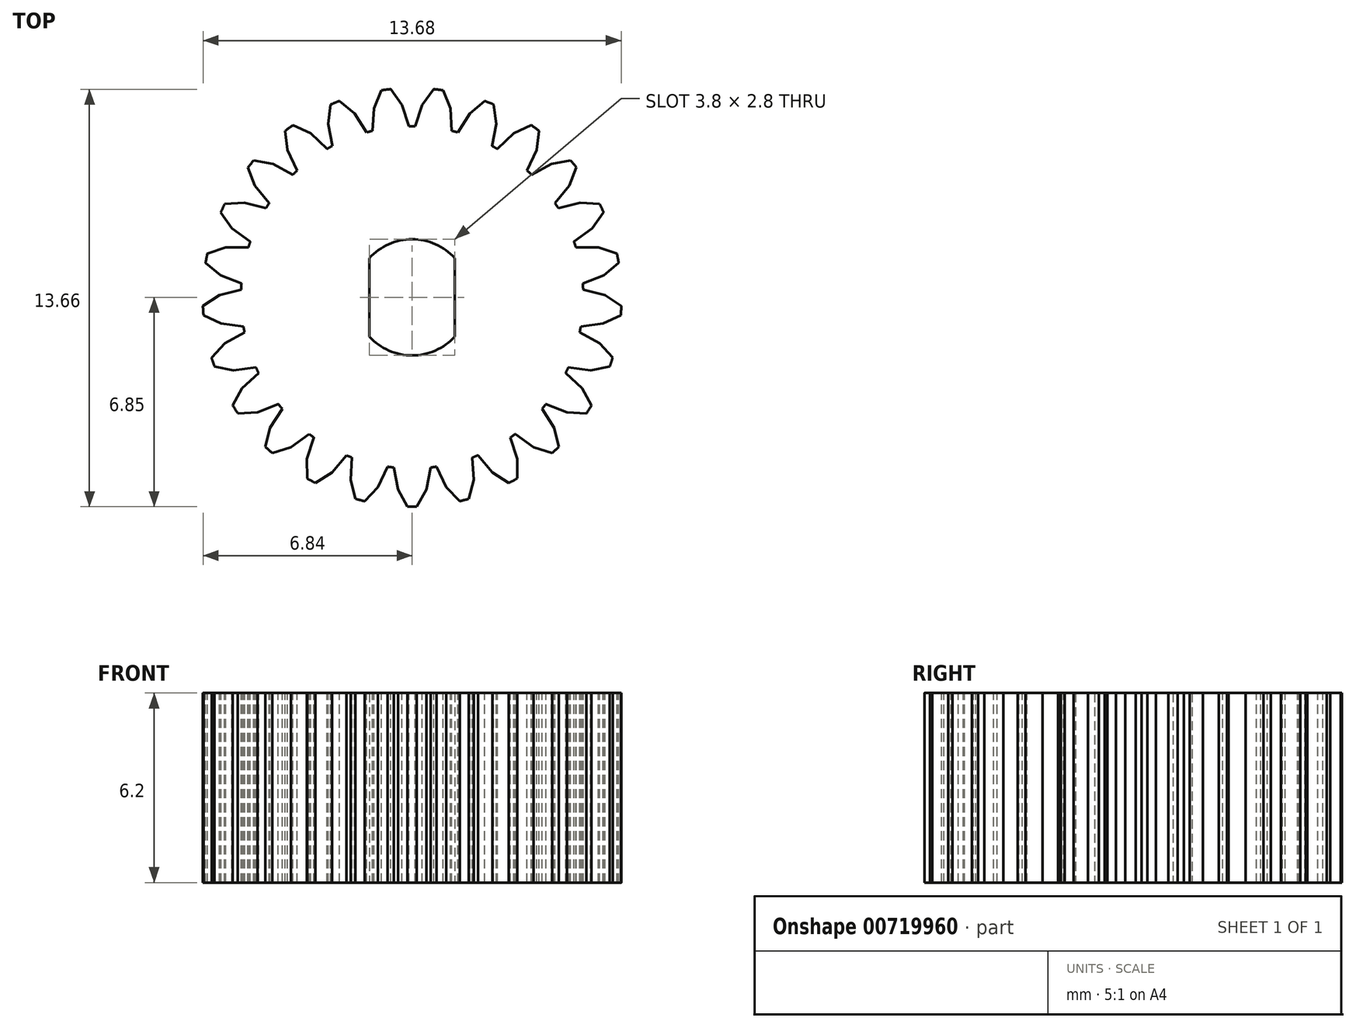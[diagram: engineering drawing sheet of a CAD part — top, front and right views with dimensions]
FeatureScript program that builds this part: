
annotation { "Feature Type Name" : "Feature", "Feature Type Description" : "" }
export const myFeature = defineFeature(function(context is Context, id is Id, definition is map)
    precondition{}
    {
        {
            var Q0;
            Q0=qCreatedBy(makeId("Top.planeOp"),FACE);
            var sketch = newSketch(context, id + "F0", { "sketchPlane" : qUnion([Q0])});
            skCircle(sketch, "E0", {"center": v(0, 0) * mm, "radius": 6.85 * mm});
            skArc(sketch, "E1", {"start": v(-1.4, -1.28) * mm, "mid": v(0, -1.9) * mm, "end": v(1.4, -1.28) * mm});
            skLineSegment(sketch, "E2.left", {"start": v(-1.4, 1.28) * mm, "end": v(-1.4, -1.28) * mm});
            skLineSegment(sketch, "E2.right", {"start": v(1.4, 1.28) * mm, "end": v(1.4, -1.28) * mm});
            skArc(sketch, "E3.trimOffspring", {"start": v(1.4, 1.28) * mm, "mid": v(0, 1.9) * mm, "end": v(-1.4, 1.28) * mm});
            skSolve(sketch);
        }
        {
            var Q0;
            Q0 = qSketchRegion(id + "F0", true);
            extrude(context, id + "F1", {"entities" : qUnion([Q0]), "depth" : 6.2 * mm, "offsetDistance" : 25 * mm});
        }
        {
            var Q0;
            Q0=makeQuery(id+"F1.opExtrude","CAP_FACE",FACE,{"disambiguationData":[OSD([sQuery(id+"F0.wireOp",EDGE,"E0"),sQuery(id+"F0.wireOp",EDGE,"E1"),sQuery(id+"F0.wireOp",EDGE,"E2.left"),sQuery(id+"F0.wireOp",EDGE,"E2.right"),sQuery(id+"F0.wireOp",EDGE,"E3.trimOffspring")])],"isStart":false});
            var sketch = newSketch(context, id + "F2", { "sketchPlane" : qUnion([Q0])});
            skArc(sketch, "E4.0", {"start": v(0.7, 6.81) * mm, "mid": v(0, 6.85) * mm, "end": v(-0.7, 6.81) * mm});
            skPoint(sketch, "E5.orphan", {"position": v(0, 5.3) * mm});
            skArc(sketch, "E6.trimOffspring", {"start": v(0.1, 5.6) * mm, "mid": v(0, 5.6) * mm, "end": v(-0.1, 5.6) * mm});
            skLineSegment(sketch, "E7", {"start": v(-0.7, 6.81) * mm, "end": v(-0.33, 6.3) * mm});
            skLineSegment(sketch, "E8", {"start": v(-0.1, 5.6) * mm, "end": v(-0.33, 6.3) * mm});
            skLineSegment(sketch, "E9.MirrorCS", {"start": v(0.7, 6.81) * mm, "end": v(0.33, 6.3) * mm});
            skLineSegment(sketch, "E10.MirrorCS", {"start": v(0.1, 5.6) * mm, "end": v(0.33, 6.3) * mm});
            skLineSegment(sketch, "E11.1.0", {"start": v(-2.38, 6.42) * mm, "end": v(-1.88, 6.02) * mm});
            skArc(sketch, "E11.1.1", {"start": v(-1.01, 6.78) * mm, "mid": v(-1.7, 6.63) * mm, "end": v(-2.38, 6.42) * mm});
            skLineSegment(sketch, "E11.1.2", {"start": v(-1.01, 6.78) * mm, "end": v(-1.25, 6.18) * mm});
            skLineSegment(sketch, "E11.1.3", {"start": v(-1.3, 5.45) * mm, "end": v(-1.25, 6.18) * mm});
            skLineSegment(sketch, "E11.1.4", {"start": v(-1.49, 5.4) * mm, "end": v(-1.88, 6.02) * mm});
            skArc(sketch, "E11.1.5", {"start": v(-1.22, 5.47) * mm, "mid": v(-1.35, 5.43) * mm, "end": v(-1.49, 5.4) * mm});
            skLineSegment(sketch, "E11.2.0", {"start": v(-3.9, 5.63) * mm, "end": v(-3.32, 5.36) * mm});
            skArc(sketch, "E11.2.1", {"start": v(-2.66, 6.31) * mm, "mid": v(-3.3, 6) * mm, "end": v(-3.9, 5.63) * mm});
            skLineSegment(sketch, "E11.2.2", {"start": v(-2.66, 6.31) * mm, "end": v(-2.75, 5.68) * mm});
            skLineSegment(sketch, "E11.2.3", {"start": v(-2.6, 4.95) * mm, "end": v(-2.75, 5.68) * mm});
            skLineSegment(sketch, "E11.2.4", {"start": v(-2.78, 4.86) * mm, "end": v(-3.32, 5.36) * mm});
            skArc(sketch, "E11.2.5", {"start": v(-2.54, 5) * mm, "mid": v(-2.66, 4.93) * mm, "end": v(-2.78, 4.86) * mm});
            skLineSegment(sketch, "E11.3.0", {"start": v(-5.18, 4.48) * mm, "end": v(-4.55, 4.37) * mm});
            skArc(sketch, "E11.3.1", {"start": v(-4.15, 5.45) * mm, "mid": v(-4.69, 5) * mm, "end": v(-5.18, 4.48) * mm});
            skLineSegment(sketch, "E11.3.2", {"start": v(-4.15, 5.45) * mm, "end": v(-4.07, 4.82) * mm});
            skLineSegment(sketch, "E11.3.3", {"start": v(-3.76, 4.15) * mm, "end": v(-4.07, 4.82) * mm});
            skLineSegment(sketch, "E11.3.4", {"start": v(-3.9, 4.01) * mm, "end": v(-4.55, 4.37) * mm});
            skArc(sketch, "E11.3.5", {"start": v(-3.7, 4.2) * mm, "mid": v(-3.8, 4.1) * mm, "end": v(-3.9, 4.01) * mm});
            skLineSegment(sketch, "E11.4.0", {"start": v(-6.13, 3.05) * mm, "end": v(-5.5, 3.1) * mm});
            skArc(sketch, "E11.4.1", {"start": v(-5.37, 4.25) * mm, "mid": v(-5.78, 3.67) * mm, "end": v(-6.13, 3.05) * mm});
            skLineSegment(sketch, "E11.4.2", {"start": v(-5.37, 4.25) * mm, "end": v(-5.14, 3.65) * mm});
            skLineSegment(sketch, "E11.4.3", {"start": v(-4.67, 3.08) * mm, "end": v(-5.14, 3.65) * mm});
            skLineSegment(sketch, "E11.4.4", {"start": v(-4.78, 2.92) * mm, "end": v(-5.5, 3.1) * mm});
            skArc(sketch, "E11.4.5", {"start": v(-4.63, 3.15) * mm, "mid": v(-4.7, 3.03) * mm, "end": v(-4.78, 2.92) * mm});
            skLineSegment(sketch, "E11.5.0", {"start": v(-6.7, 1.43) * mm, "end": v(-6.1, 1.63) * mm});
            skArc(sketch, "E11.5.1", {"start": v(-6.26, 2.78) * mm, "mid": v(-6.51, 2.12) * mm, "end": v(-6.7, 1.43) * mm});
            skLineSegment(sketch, "E11.5.2", {"start": v(-6.26, 2.78) * mm, "end": v(-5.9, 2.26) * mm});
            skLineSegment(sketch, "E11.5.3", {"start": v(-5.3, 1.83) * mm, "end": v(-5.9, 2.26) * mm});
            skLineSegment(sketch, "E11.5.4", {"start": v(-5.36, 1.63) * mm, "end": v(-6.1, 1.63) * mm});
            skArc(sketch, "E11.5.5", {"start": v(-5.27, 1.9) * mm, "mid": v(-5.31, 1.77) * mm, "end": v(-5.36, 1.63) * mm});
            skLineSegment(sketch, "E11.6.0", {"start": v(-6.84, -0.28) * mm, "end": v(-6.3, 0.07) * mm});
            skArc(sketch, "E11.6.1", {"start": v(-6.76, 1.13) * mm, "mid": v(-6.84, 0.43) * mm, "end": v(-6.84, -0.28) * mm});
            skLineSegment(sketch, "E11.6.2", {"start": v(-6.76, 1.13) * mm, "end": v(-6.27, 0.72) * mm});
            skLineSegment(sketch, "E11.6.3", {"start": v(-5.58, 0.45) * mm, "end": v(-6.27, 0.72) * mm});
            skLineSegment(sketch, "E11.6.4", {"start": v(-5.6, 0.25) * mm, "end": v(-6.3, 0.07) * mm});
            skArc(sketch, "E11.6.5", {"start": v(-5.58, 0.53) * mm, "mid": v(-5.59, 0.4) * mm, "end": v(-5.6, 0.25) * mm});
            skLineSegment(sketch, "E11.7.0", {"start": v(-6.56, -1.97) * mm, "end": v(-6.13, -1.5) * mm});
            skArc(sketch, "E11.7.1", {"start": v(-6.83, -0.58) * mm, "mid": v(-6.73, -1.28) * mm, "end": v(-6.56, -1.97) * mm});
            skLineSegment(sketch, "E11.7.2", {"start": v(-6.83, -0.58) * mm, "end": v(-6.25, -0.86) * mm});
            skLineSegment(sketch, "E11.7.3", {"start": v(-5.52, -0.95) * mm, "end": v(-6.25, -0.86) * mm});
            skLineSegment(sketch, "E11.7.4", {"start": v(-5.48, -1.15) * mm, "end": v(-6.13, -1.5) * mm});
            skArc(sketch, "E11.7.5", {"start": v(-5.53, -0.87) * mm, "mid": v(-5.5, -1.01) * mm, "end": v(-5.48, -1.15) * mm});
            skLineSegment(sketch, "E11.8.0", {"start": v(-5.86, -3.54) * mm, "end": v(-5.56, -2.98) * mm});
            skArc(sketch, "E11.8.1", {"start": v(-6.47, -2.26) * mm, "mid": v(-6.2, -2.92) * mm, "end": v(-5.86, -3.54) * mm});
            skLineSegment(sketch, "E11.8.2", {"start": v(-6.47, -2.26) * mm, "end": v(-5.84, -2.39) * mm});
            skLineSegment(sketch, "E11.8.3", {"start": v(-5.1, -2.3) * mm, "end": v(-5.84, -2.39) * mm});
            skLineSegment(sketch, "E11.8.4", {"start": v(-5.02, -2.47) * mm, "end": v(-5.56, -2.98) * mm});
            skArc(sketch, "E11.8.5", {"start": v(-5.14, -2.22) * mm, "mid": v(-5.08, -2.35) * mm, "end": v(-5.02, -2.47) * mm});
            skLineSegment(sketch, "E11.9.0", {"start": v(-4.8, -4.89) * mm, "end": v(-4.65, -4.27) * mm});
            skArc(sketch, "E11.9.1", {"start": v(-5.7, -3.8) * mm, "mid": v(-5.28, -4.37) * mm, "end": v(-4.8, -4.89) * mm});
            skLineSegment(sketch, "E11.9.2", {"start": v(-5.7, -3.8) * mm, "end": v(-5.06, -3.76) * mm});
            skLineSegment(sketch, "E11.9.3", {"start": v(-4.38, -3.5) * mm, "end": v(-5.06, -3.76) * mm});
            skLineSegment(sketch, "E11.9.4", {"start": v(-4.25, -3.65) * mm, "end": v(-4.65, -4.27) * mm});
            skArc(sketch, "E11.9.5", {"start": v(-4.43, -3.43) * mm, "mid": v(-4.34, -3.54) * mm, "end": v(-4.25, -3.65) * mm});
            skLineSegment(sketch, "E11.10.0", {"start": v(-3.43, -5.93) * mm, "end": v(-3.44, -5.29) * mm});
            skArc(sketch, "E11.10.1", {"start": v(-4.58, -5.1) * mm, "mid": v(-4.03, -5.54) * mm, "end": v(-3.43, -5.93) * mm});
            skLineSegment(sketch, "E11.10.2", {"start": v(-4.58, -5.1) * mm, "end": v(-3.97, -4.9) * mm});
            skLineSegment(sketch, "E11.10.3", {"start": v(-3.37, -4.47) * mm, "end": v(-3.97, -4.9) * mm});
            skLineSegment(sketch, "E11.10.4", {"start": v(-3.2, -4.59) * mm, "end": v(-3.44, -5.29) * mm});
            skArc(sketch, "E11.10.5", {"start": v(-3.43, -4.42) * mm, "mid": v(-3.32, -4.5) * mm, "end": v(-3.2, -4.59) * mm});
            skLineSegment(sketch, "E11.11.0", {"start": v(-1.85, -6.6) * mm, "end": v(-2.01, -5.98) * mm});
            skArc(sketch, "E11.11.1", {"start": v(-3.16, -6.08) * mm, "mid": v(-2.52, -6.37) * mm, "end": v(-1.85, -6.6) * mm});
            skLineSegment(sketch, "E11.11.2", {"start": v(-3.16, -6.08) * mm, "end": v(-2.62, -5.74) * mm});
            skLineSegment(sketch, "E11.11.3", {"start": v(-2.15, -5.17) * mm, "end": v(-2.62, -5.74) * mm});
            skLineSegment(sketch, "E11.11.4", {"start": v(-1.97, -5.24) * mm, "end": v(-2.01, -5.98) * mm});
            skArc(sketch, "E11.11.5", {"start": v(-2.23, -5.14) * mm, "mid": v(-2.1, -5.2) * mm, "end": v(-1.97, -5.24) * mm});
            skLineSegment(sketch, "E11.12.0", {"start": v(-0.15, -6.85) * mm, "end": v(-0.46, -6.3) * mm});
            skArc(sketch, "E11.12.1", {"start": v(-1.55, -6.67) * mm, "mid": v(-0.86, -6.8) * mm, "end": v(-0.15, -6.85) * mm});
            skLineSegment(sketch, "E11.12.2", {"start": v(-1.55, -6.67) * mm, "end": v(-1.12, -6.2) * mm});
            skLineSegment(sketch, "E11.12.3", {"start": v(-0.8, -5.54) * mm, "end": v(-1.12, -6.2) * mm});
            skLineSegment(sketch, "E11.12.4", {"start": v(-0.6, -5.57) * mm, "end": v(-0.46, -6.3) * mm});
            skArc(sketch, "E11.12.5", {"start": v(-0.88, -5.53) * mm, "mid": v(-0.74, -5.55) * mm, "end": v(-0.6, -5.57) * mm});
            skLineSegment(sketch, "E11.13.0", {"start": v(1.55, -6.67) * mm, "end": v(1.12, -6.2) * mm});
            skArc(sketch, "E11.13.1", {"start": v(0.15, -6.85) * mm, "mid": v(0.86, -6.8) * mm, "end": v(1.55, -6.67) * mm});
            skLineSegment(sketch, "E11.13.2", {"start": v(0.15, -6.85) * mm, "end": v(0.46, -6.3) * mm});
            skLineSegment(sketch, "E11.13.3", {"start": v(0.6, -5.57) * mm, "end": v(0.46, -6.3) * mm});
            skLineSegment(sketch, "E11.13.4", {"start": v(0.8, -5.54) * mm, "end": v(1.12, -6.2) * mm});
            skArc(sketch, "E11.13.5", {"start": v(0.52, -5.58) * mm, "mid": v(0.66, -5.56) * mm, "end": v(0.8, -5.54) * mm});
            skLineSegment(sketch, "E11.14.0", {"start": v(3.16, -6.08) * mm, "end": v(2.62, -5.74) * mm});
            skArc(sketch, "E11.14.1", {"start": v(1.85, -6.6) * mm, "mid": v(2.52, -6.37) * mm, "end": v(3.16, -6.08) * mm});
            skLineSegment(sketch, "E11.14.2", {"start": v(1.85, -6.6) * mm, "end": v(2.01, -5.98) * mm});
            skLineSegment(sketch, "E11.14.3", {"start": v(1.97, -5.24) * mm, "end": v(2.01, -5.98) * mm});
            skLineSegment(sketch, "E11.14.4", {"start": v(2.15, -5.17) * mm, "end": v(2.62, -5.74) * mm});
            skArc(sketch, "E11.14.5", {"start": v(1.9, -5.27) * mm, "mid": v(2.03, -5.22) * mm, "end": v(2.15, -5.17) * mm});
            skLineSegment(sketch, "E11.15.0", {"start": v(4.58, -5.1) * mm, "end": v(3.97, -4.9) * mm});
            skArc(sketch, "E11.15.1", {"start": v(3.43, -5.93) * mm, "mid": v(4.03, -5.54) * mm, "end": v(4.58, -5.1) * mm});
            skLineSegment(sketch, "E11.15.2", {"start": v(3.43, -5.93) * mm, "end": v(3.44, -5.29) * mm});
            skLineSegment(sketch, "E11.15.3", {"start": v(3.2, -4.59) * mm, "end": v(3.44, -5.29) * mm});
            skLineSegment(sketch, "E11.15.4", {"start": v(3.37, -4.47) * mm, "end": v(3.97, -4.9) * mm});
            skArc(sketch, "E11.15.5", {"start": v(3.15, -4.63) * mm, "mid": v(3.26, -4.55) * mm, "end": v(3.37, -4.47) * mm});
            skLineSegment(sketch, "E11.16.0", {"start": v(5.7, -3.8) * mm, "end": v(5.06, -3.76) * mm});
            skArc(sketch, "E11.16.1", {"start": v(4.8, -4.89) * mm, "mid": v(5.28, -4.37) * mm, "end": v(5.7, -3.8) * mm});
            skLineSegment(sketch, "E11.16.2", {"start": v(4.8, -4.89) * mm, "end": v(4.65, -4.27) * mm});
            skLineSegment(sketch, "E11.16.3", {"start": v(4.25, -3.65) * mm, "end": v(4.65, -4.27) * mm});
            skLineSegment(sketch, "E11.16.4", {"start": v(4.38, -3.5) * mm, "end": v(5.06, -3.76) * mm});
            skArc(sketch, "E11.16.5", {"start": v(4.2, -3.7) * mm, "mid": v(4.29, -3.6) * mm, "end": v(4.38, -3.5) * mm});
            skLineSegment(sketch, "E11.17.0", {"start": v(6.47, -2.26) * mm, "end": v(5.84, -2.39) * mm});
            skArc(sketch, "E11.17.1", {"start": v(5.86, -3.54) * mm, "mid": v(6.2, -2.92) * mm, "end": v(6.47, -2.26) * mm});
            skLineSegment(sketch, "E11.17.2", {"start": v(5.86, -3.54) * mm, "end": v(5.56, -2.98) * mm});
            skLineSegment(sketch, "E11.17.3", {"start": v(5.02, -2.47) * mm, "end": v(5.56, -2.98) * mm});
            skLineSegment(sketch, "E11.17.4", {"start": v(5.1, -2.3) * mm, "end": v(5.84, -2.39) * mm});
            skArc(sketch, "E11.17.5", {"start": v(4.99, -2.54) * mm, "mid": v(5.05, -2.42) * mm, "end": v(5.1, -2.3) * mm});
            skLineSegment(sketch, "E11.18.0", {"start": v(6.83, -0.58) * mm, "end": v(6.25, -0.86) * mm});
            skArc(sketch, "E11.18.1", {"start": v(6.56, -1.97) * mm, "mid": v(6.73, -1.28) * mm, "end": v(6.83, -0.58) * mm});
            skLineSegment(sketch, "E11.18.2", {"start": v(6.56, -1.97) * mm, "end": v(6.13, -1.5) * mm});
            skLineSegment(sketch, "E11.18.3", {"start": v(5.48, -1.15) * mm, "end": v(6.13, -1.5) * mm});
            skLineSegment(sketch, "E11.18.4", {"start": v(5.52, -0.95) * mm, "end": v(6.25, -0.86) * mm});
            skArc(sketch, "E11.18.5", {"start": v(5.47, -1.22) * mm, "mid": v(5.5, -1.09) * mm, "end": v(5.52, -0.95) * mm});
            skLineSegment(sketch, "E11.19.0", {"start": v(6.76, 1.13) * mm, "end": v(6.27, 0.72) * mm});
            skArc(sketch, "E11.19.1", {"start": v(6.84, -0.28) * mm, "mid": v(6.84, 0.43) * mm, "end": v(6.76, 1.13) * mm});
            skLineSegment(sketch, "E11.19.2", {"start": v(6.84, -0.28) * mm, "end": v(6.3, 0.07) * mm});
            skLineSegment(sketch, "E11.19.3", {"start": v(5.6, 0.25) * mm, "end": v(6.3, 0.07) * mm});
            skLineSegment(sketch, "E11.19.4", {"start": v(5.58, 0.45) * mm, "end": v(6.27, 0.72) * mm});
            skArc(sketch, "E11.19.5", {"start": v(5.6, 0.17) * mm, "mid": v(5.6, 0.31) * mm, "end": v(5.58, 0.45) * mm});
            skLineSegment(sketch, "E11.20.0", {"start": v(6.26, 2.78) * mm, "end": v(5.9, 2.26) * mm});
            skArc(sketch, "E11.20.1", {"start": v(6.7, 1.43) * mm, "mid": v(6.51, 2.12) * mm, "end": v(6.26, 2.78) * mm});
            skLineSegment(sketch, "E11.20.2", {"start": v(6.7, 1.43) * mm, "end": v(6.1, 1.63) * mm});
            skLineSegment(sketch, "E11.20.3", {"start": v(5.36, 1.63) * mm, "end": v(6.1, 1.63) * mm});
            skLineSegment(sketch, "E11.20.4", {"start": v(5.3, 1.83) * mm, "end": v(5.9, 2.26) * mm});
            skArc(sketch, "E11.20.5", {"start": v(5.38, 1.56) * mm, "mid": v(5.34, 1.7) * mm, "end": v(5.3, 1.83) * mm});
            skLineSegment(sketch, "E11.21.0", {"start": v(5.37, 4.25) * mm, "end": v(5.14, 3.65) * mm});
            skArc(sketch, "E11.21.1", {"start": v(6.13, 3.05) * mm, "mid": v(5.78, 3.67) * mm, "end": v(5.37, 4.25) * mm});
            skLineSegment(sketch, "E11.21.2", {"start": v(6.13, 3.05) * mm, "end": v(5.5, 3.1) * mm});
            skLineSegment(sketch, "E11.21.3", {"start": v(4.78, 2.92) * mm, "end": v(5.5, 3.1) * mm});
            skLineSegment(sketch, "E11.21.4", {"start": v(4.67, 3.08) * mm, "end": v(5.14, 3.65) * mm});
            skArc(sketch, "E11.21.5", {"start": v(4.82, 2.85) * mm, "mid": v(4.75, 2.97) * mm, "end": v(4.67, 3.08) * mm});
            skLineSegment(sketch, "E11.22.0", {"start": v(4.15, 5.45) * mm, "end": v(4.07, 4.82) * mm});
            skArc(sketch, "E11.22.1", {"start": v(5.18, 4.48) * mm, "mid": v(4.69, 5) * mm, "end": v(4.15, 5.45) * mm});
            skLineSegment(sketch, "E11.22.2", {"start": v(5.18, 4.48) * mm, "end": v(4.55, 4.37) * mm});
            skLineSegment(sketch, "E11.22.3", {"start": v(3.9, 4.01) * mm, "end": v(4.55, 4.37) * mm});
            skLineSegment(sketch, "E11.22.4", {"start": v(3.76, 4.15) * mm, "end": v(4.07, 4.82) * mm});
            skArc(sketch, "E11.22.5", {"start": v(3.96, 3.96) * mm, "mid": v(3.86, 4.06) * mm, "end": v(3.76, 4.15) * mm});
            skLineSegment(sketch, "E11.23.0", {"start": v(2.66, 6.31) * mm, "end": v(2.75, 5.68) * mm});
            skArc(sketch, "E11.23.1", {"start": v(3.9, 5.63) * mm, "mid": v(3.3, 6) * mm, "end": v(2.66, 6.31) * mm});
            skLineSegment(sketch, "E11.23.2", {"start": v(3.9, 5.63) * mm, "end": v(3.32, 5.36) * mm});
            skLineSegment(sketch, "E11.23.3", {"start": v(2.78, 4.86) * mm, "end": v(3.32, 5.36) * mm});
            skLineSegment(sketch, "E11.23.4", {"start": v(2.6, 4.95) * mm, "end": v(2.75, 5.68) * mm});
            skArc(sketch, "E11.23.5", {"start": v(2.85, 4.82) * mm, "mid": v(2.73, 4.89) * mm, "end": v(2.6, 4.95) * mm});
            skLineSegment(sketch, "E11.24.0", {"start": v(1.01, 6.78) * mm, "end": v(1.25, 6.18) * mm});
            skArc(sketch, "E11.24.1", {"start": v(2.38, 6.42) * mm, "mid": v(1.7, 6.63) * mm, "end": v(1.01, 6.78) * mm});
            skLineSegment(sketch, "E11.24.2", {"start": v(2.38, 6.42) * mm, "end": v(1.88, 6.02) * mm});
            skLineSegment(sketch, "E11.24.3", {"start": v(1.49, 5.4) * mm, "end": v(1.88, 6.02) * mm});
            skLineSegment(sketch, "E11.24.4", {"start": v(1.3, 5.45) * mm, "end": v(1.25, 6.18) * mm});
            skArc(sketch, "E11.24.5", {"start": v(1.56, 5.38) * mm, "mid": v(1.43, 5.41) * mm, "end": v(1.3, 5.45) * mm});
            skPoint(sketch, "E12.orphan", {"position": v(0.18, 5.6) * mm});
            skSolve(sketch);
        }
        {
            var Q0;
            Q0 = qSketchRegion(id + "F2", true);
            extrude(context, id + "F3", {"entities" : qUnion([Q0]), "operationType" : NewBodyOperationType.REMOVE, "oppositeDirection" : true, "depth" : 25 * mm, "offsetDistance" : 25 * mm});
        }
    });
